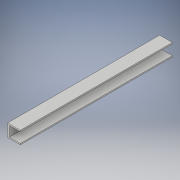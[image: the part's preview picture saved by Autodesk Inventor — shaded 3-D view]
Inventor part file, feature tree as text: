
AUTODESK INVENTOR PART (.ipt)
format: ipt  version: 2018 (Build 220112000, 112)  size: 100,864 bytes
history: native  units: in
note: dims shown in document units (in); Inventor stores cm internally (conversion verified against a paired STEP export)
features: extrude x1, sketch x1
ambient origin geometry x8: Origin, YZ Plane, XZ Plane, XY Plane, X Axis, Y Axis, Z Axis, Center Point
bodies: Solid1 (feature_tree)
feature tree (2):
  extrude  "Extrusion1"  Depth=1.5in
  sketch  "Sketch1"  dims[d0=1.5in d1=1.5in d2=1.3in d3=0.15in d4=0.15in d5=18.0in d6=0.0in]
